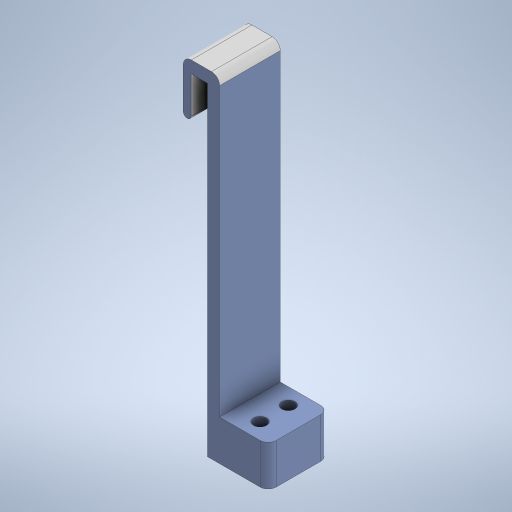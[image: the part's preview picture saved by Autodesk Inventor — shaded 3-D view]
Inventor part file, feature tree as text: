
AUTODESK INVENTOR PART (.ipt)
format: ipt  version: 2024.1 (Build 281209000, 209)  size: 284,160 bytes
history: native  units: mm
features: fillet x3, extrude x2, sketch x2
ambient origin geometry x8: Origin, YZ Plane, XZ Plane, XY Plane, X Axis, Y Axis, Z Axis, Center Point
bodies: Solide1 (feature_tree)
feature tree (7):
  extrude  "Extrusion1"  Depth=15.0mm TaperAngle=0.0deg
  extrude  "Extrusion2"  Depth=3.2mm
  fillet  "Congé2"  Radius=3.2mm
  fillet  "Congé3"  Radius=4.0mm
  fillet  "Congé4"  Radius=4.0mm
  sketch  "Esquisse1"
  sketch  "Esquisse2"
